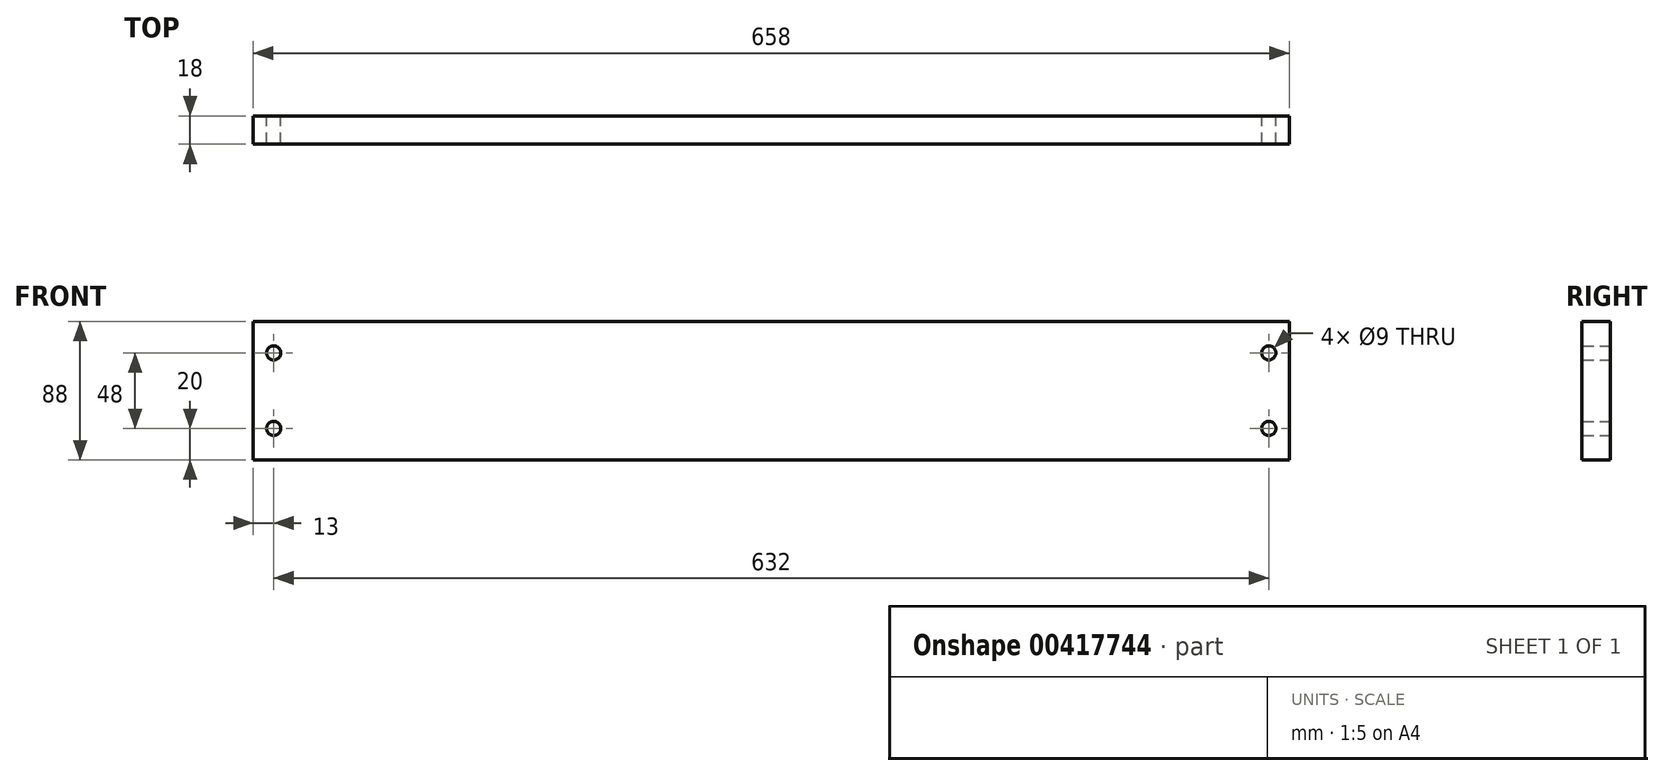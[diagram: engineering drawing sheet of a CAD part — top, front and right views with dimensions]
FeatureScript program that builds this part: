
annotation { "Feature Type Name" : "Feature", "Feature Type Description" : "" }
export const myFeature = defineFeature(function(context is Context, id is Id, definition is map)
    precondition{}
    {
        {
            var Q0;
            Q0=qCreatedBy(makeId("Right.planeOp"),FACE);
            var sketch = newSketch(context, id + "F0", { "sketchPlane" : qUnion([Q0])});
            skLineSegment(sketch, "E0.bottom", {"start": v(0, 44) * mm, "end": v(18, 44) * mm});
            skLineSegment(sketch, "E0.top", {"start": v(0, -44) * mm, "end": v(18, -44) * mm});
            skLineSegment(sketch, "E0.left", {"start": v(0, 44) * mm, "end": v(0, -44) * mm});
            skLineSegment(sketch, "E0.right", {"start": v(18, 44) * mm, "end": v(18, -44) * mm});
            skSolve(sketch);
        }
        {
            var Q0;
            Q0=qSketchRegion(id+"F0",true);
            extrude(context, id + "F1", {"entities" : qUnion([Q0]), "depth" : 329 * mm});
        }
        {
            var Q0;
            Q0=makeQuery(id+"F1.opExtrude","SWEPT_FACE",FACE,{"disambiguationData":[OSD([sQuery(id+"F0.wireOp",EDGE,"E0.right")])]});
            var sketch = newSketch(context, id + "F2", { "sketchPlane" : qUnion([Q0])});
            skLineSegment(sketch, "E1", {"start": v(-316, 44) * mm, "end": v(-316, -44) * mm, "construction": true});
            skCircle(sketch, "E2", {"center": v(-316, 24) * mm, "radius": 4.5 * mm});
            skCircle(sketch, "E3", {"center": v(-316, -24) * mm, "radius": 4.5 * mm});
            skLineSegment(sketch, "E4", {"start": v(-329, 0) * mm, "end": v(-316, 0) * mm, "construction": true});
            skSolve(sketch);
        }
        {
            var Q0;
            Q0=qSketchRegion(id+"F2",true);
            extrude(context, id + "F3", {"entities" : qUnion([Q0]), "operationType" : NewBodyOperationType.REMOVE, "endBound" : BoundingType.THROUGH_ALL, "oppositeDirection" : true, "depth" : 25 * mm});
        }
        {
            var Q0;
            Q0=makeQuery(id+"F1.opExtrude","SWEPT_BODY",BODY,{"disambiguationData":[OSD([sQuery(id+"F0.wireOp",EDGE,"E0.bottom"),sQuery(id+"F0.wireOp",EDGE,"E0.top"),sQuery(id+"F0.wireOp",EDGE,"E0.left"),sQuery(id+"F0.wireOp",EDGE,"E0.right")])]});
            var Q1;
            Q1=qCreatedBy(makeId("Right.planeOp"),FACE);
            mirror(context, id + "F4", {"operationType" : NewBodyOperationType.ADD, "entities" : qUnion([Q0]), "mirrorPlane" : qUnion([Q1])});
        }
    });
